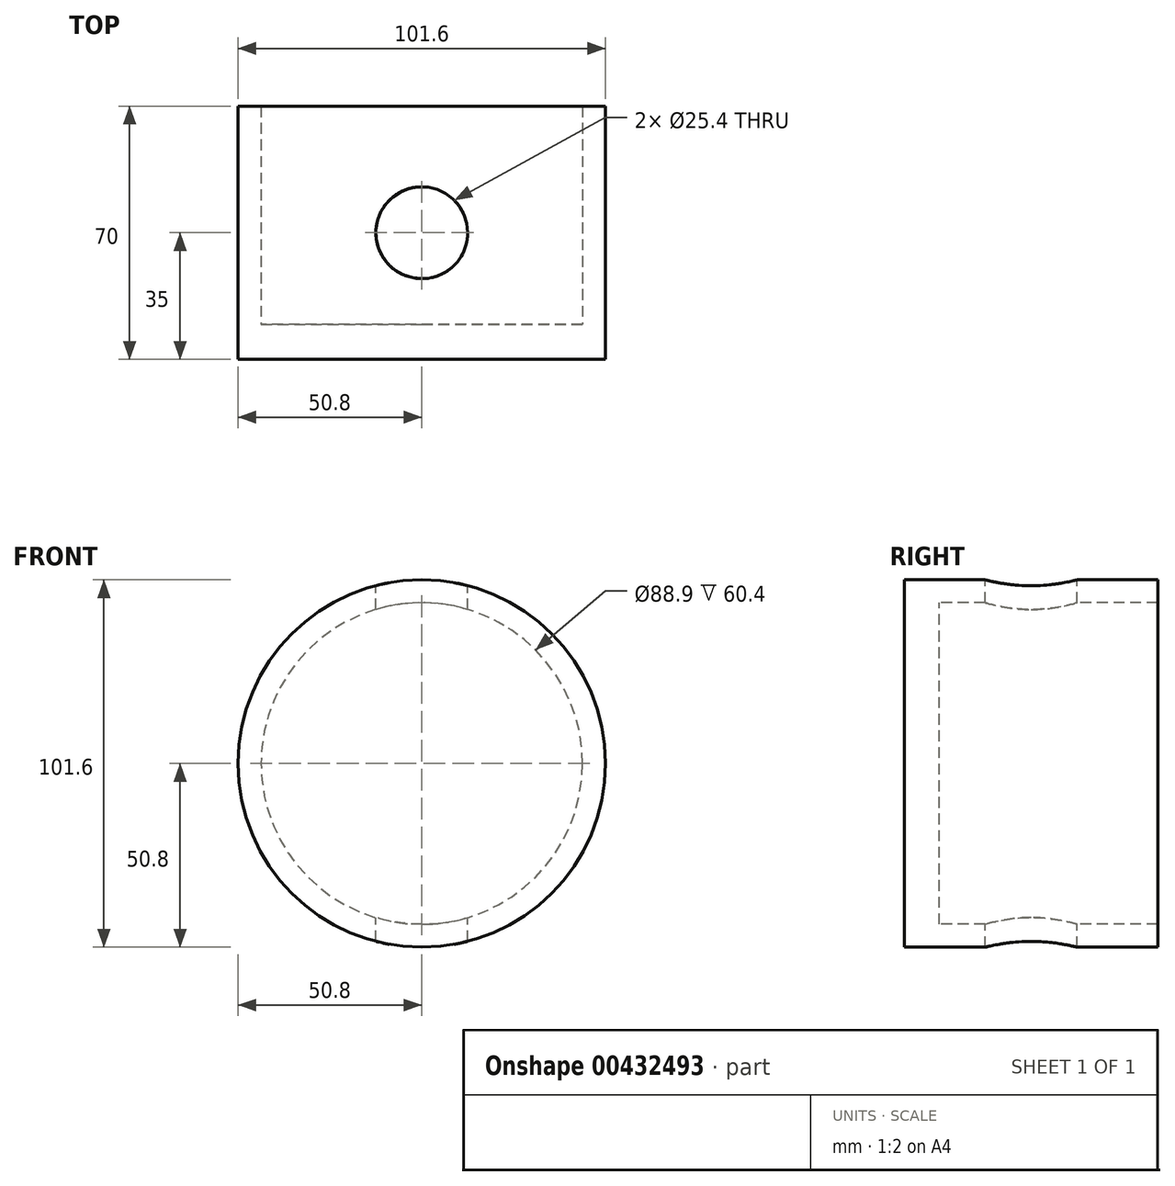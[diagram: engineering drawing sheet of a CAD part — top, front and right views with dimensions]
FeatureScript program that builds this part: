
annotation { "Feature Type Name" : "Feature", "Feature Type Description" : "" }
export const myFeature = defineFeature(function(context is Context, id is Id, definition is map)
    precondition{}
    {
        {
            var Q0;
            Q0=qCreatedBy(makeId("Front.planeOp"),FACE);
            var sketch = newSketch(context, id + "F0", { "sketchPlane" : qUnion([Q0])});
            skCircle(sketch, "E0", {"center": v(0, 0) * mm, "radius": 50.8 * mm});
            skSolve(sketch);
        }
        {
            var Q0;
            Q0 = qSketchRegion(id + "F0", true);
            extrude(context, id + "F1", {"entities" : qUnion([Q0]), "endBound" : BoundingType.SYMMETRIC, "depth" : 70 * mm});
        }
        {
            var Q0;
            Q0=qCreatedBy(makeId("Front.planeOp"),FACE);
            var sketch = newSketch(context, id + "F2", { "sketchPlane" : qUnion([Q0])});
            skCircle(sketch, "E1", {"center": v(0, 0) * mm, "radius": 44.45 * mm});
            skSolve(sketch);
        }
        {
            var Q0;
            Q0 = qSketchRegion(id + "F2", true);
            extrude(context, id + "F3", {"entities" : qUnion([Q0]), "operationType" : NewBodyOperationType.REMOVE, "oppositeDirection" : true, "depth" : 82.56 * mm});
        }
        {
            var Q0;
            Q0=makeQuery(id+"F3.boolean.opBoolean","COPY",FACE,{"derivedFrom":makeQuery(id+"F3.opExtrude","CAP_FACE",FACE,{"disambiguationData":[OSD([sQuery(id+"F2.wireOp",EDGE,"E1")])],"isStart":true})});
            extrude(context, id + "F4", {"entities" : qUnion([Q0]), "operationType" : NewBodyOperationType.REMOVE, "oppositeDirection" : true, "depth" : 25.4 * mm});
        }
        {
            var Q0;
            Q0=qCreatedBy(makeId("Top.planeOp"),FACE);
            var sketch = newSketch(context, id + "F5", { "sketchPlane" : qUnion([Q0])});
            skCircle(sketch, "E2", {"center": v(0, 0) * mm, "radius": 12.7 * mm});
            skSolve(sketch);
        }
        {
            var Q0;
            Q0 = qSketchRegion(id + "F5", true);
            extrude(context, id + "F6", {"entities" : qUnion([Q0]), "operationType" : NewBodyOperationType.REMOVE, "endBound" : BoundingType.SYMMETRIC, "oppositeDirection" : true, "depth" : 142.44 * mm});
        }
    });
